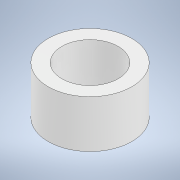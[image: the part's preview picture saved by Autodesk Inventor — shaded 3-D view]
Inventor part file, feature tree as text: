
AUTODESK INVENTOR PART (.ipt)
format: ipt  version: 2022.2 (Build 262287000, 287)  size: 100,352 bytes
history: native  units: in
note: dims shown in document units (in); Inventor stores cm internally (conversion verified against a paired STEP export)
features: extrude x1, sketch x1
ambient origin geometry x8: Origin, YZ Plane, XZ Plane, XY Plane, X Axis, Y Axis, Z Axis, Center Point
bodies: Solid1 (feature_tree)
feature tree (2):
  extrude  "Extrusion1"  Depth=0.625in
  sketch  "Sketch1"  dims[d0=0.74in d1=1.1in d2=0.625in d3=0.0in]
